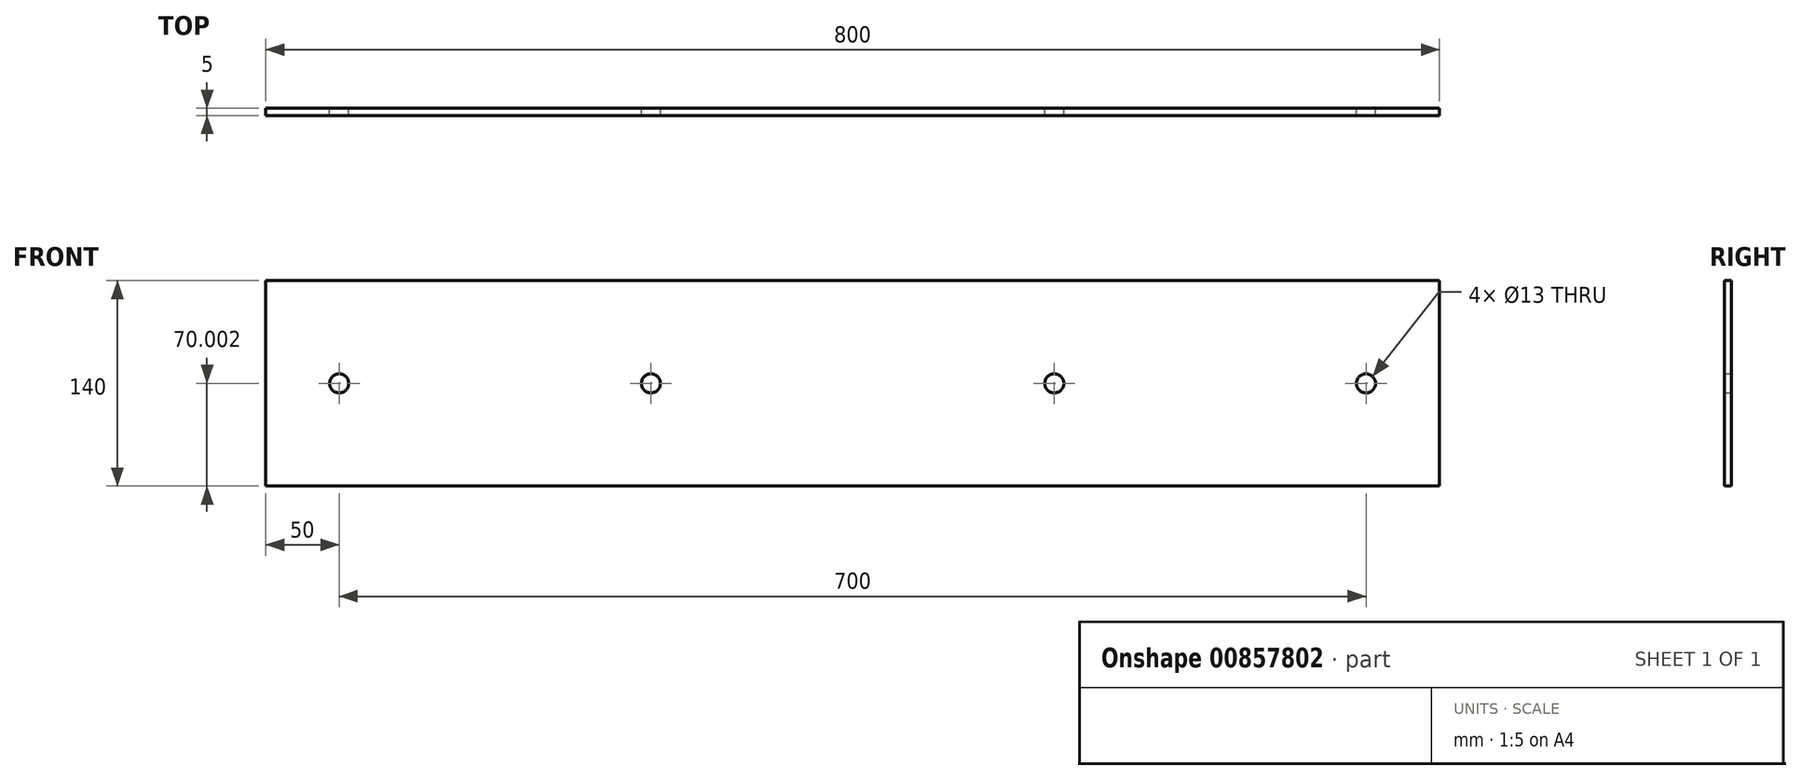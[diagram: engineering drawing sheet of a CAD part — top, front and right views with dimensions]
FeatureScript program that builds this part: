
annotation { "Feature Type Name" : "Feature", "Feature Type Description" : "" }
export const myFeature = defineFeature(function(context is Context, id is Id, definition is map)
    precondition{}
    {
        {
            var Q0;
            Q0=qCreatedBy(makeId("Front.planeOp"),FACE);
            var sketch = newSketch(context, id + "F0", { "sketchPlane" : qUnion([Q0])});
            skLineSegment(sketch, "E0", {"start": v(326.03, 294.16) * mm, "end": v(326.03, 154.16) * mm});
            skCircle(sketch, "E1", {"center": v(276.03, 224.16) * mm, "radius": 6.5 * mm});
            skCircle(sketch, "E2", {"center": v(63.53, 224.16) * mm, "radius": 6.5 * mm});
            skLineSegment(sketch, "E3.MirrorCS", {"start": v(-473.97, 294.16) * mm, "end": v(-473.97, 154.16) * mm});
            skCircle(sketch, "E4.MirrorC", {"center": v(-211.47, 224.16) * mm, "radius": 6.5 * mm});
            skCircle(sketch, "E5.MirrorC", {"center": v(-423.97, 224.16) * mm, "radius": 6.5 * mm});
            skLineSegment(sketch, "E6", {"start": v(326.03, 294.16) * mm, "end": v(-473.97, 294.16) * mm});
            skLineSegment(sketch, "E7", {"start": v(-473.97, 154.16) * mm, "end": v(326.03, 154.16) * mm});
            skSolve(sketch);
        }
        {
            var Q0;
            Q0=makeQuery(id+"F0.imprint","IMPRINT",FACE,{"disambiguationData":[TD([[makeQuery(id+"F0.imprint","IMPRINT",EDGE,{"derivedFrom":sQuery(id+"F0.wireOp",EDGE,"E0")}),-1.0]])]});
            extrude(context, id + "F1", {"entities" : qUnion([Q0]), "depth" : 5 * mm, "offsetDistance" : 25 * mm});
        }
    });
